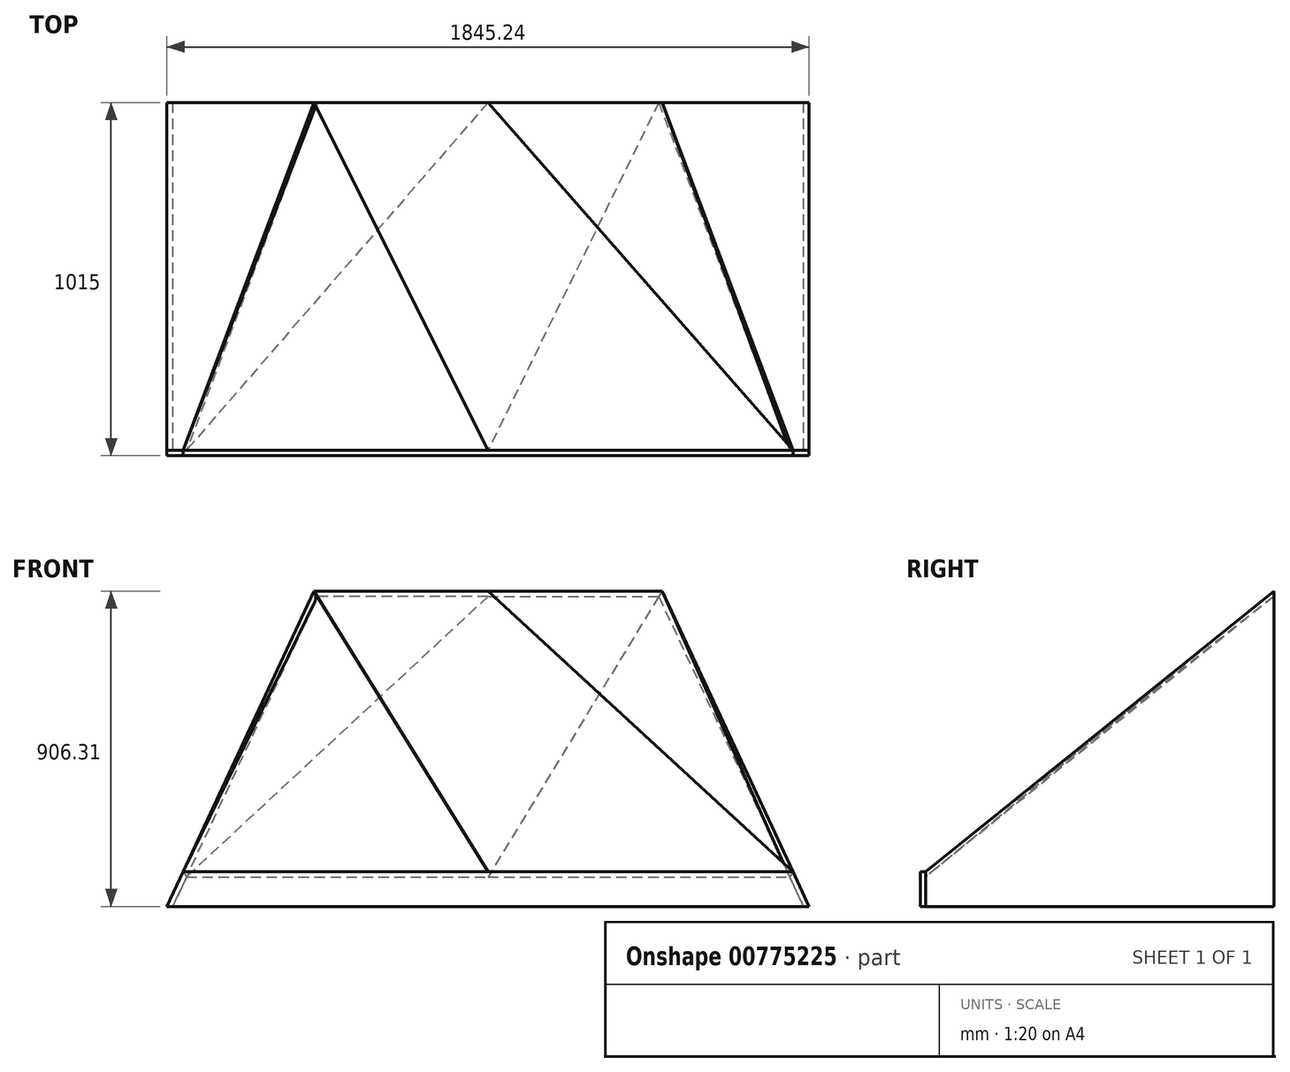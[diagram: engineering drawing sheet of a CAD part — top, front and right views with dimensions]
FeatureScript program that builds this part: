
annotation { "Feature Type Name" : "Feature", "Feature Type Description" : "" }
export const myFeature = defineFeature(function(context is Context, id is Id, definition is map)
    precondition{}
    {
        {
            var Q0;
            Q0=qCreatedBy(makeId("Front.planeOp"),FACE);
            cPlane(context, id + "F0", {"entities" : qUnion([Q0]), "cplaneType" : CPlaneType.OFFSET, "offset" : 1000 * mm, "width" : 150 * mm, "height" : 150 * mm});
        }
        {
            var Q0;
            Q0=qCreatedBy(makeId("Front.planeOp"),FACE);
            var sketch = newSketch(context, id + "F1", { "sketchPlane" : qUnion([Q0])});
            skLineSegment(sketch, "E0", {"start": v(0, 0) * mm, "end": v(-500, 0) * mm});
            skLineSegment(sketch, "E1", {"start": v(-500, 0) * mm, "end": v(-922.62, -906.3) * mm});
            skLineSegment(sketch, "E2", {"start": v(-922.62, -906.3) * mm, "end": v(0, -906.3) * mm});
            skLineSegment(sketch, "E3.MirrorCS", {"start": v(0, 0) * mm, "end": v(500, 0) * mm});
            skLineSegment(sketch, "E4.MirrorCS", {"start": v(500, 0) * mm, "end": v(922.62, -906.3) * mm});
            skLineSegment(sketch, "E5.MirrorCS", {"start": v(922.62, -906.3) * mm, "end": v(0, -906.3) * mm});
            skLineSegment(sketch, "E6.0", {"start": v(-490.44, -15) * mm, "end": v(-906.07, -906.3) * mm});
            skLineSegment(sketch, "E6.1", {"start": v(0, -15) * mm, "end": v(-490.44, -15) * mm});
            skLineSegment(sketch, "E6.2", {"start": v(0, -15) * mm, "end": v(490.44, -15) * mm});
            skLineSegment(sketch, "E6.3", {"start": v(490.44, -15) * mm, "end": v(906.07, -906.3) * mm});
            skLineSegment(sketch, "E7", {"start": v(-500, 0) * mm, "end": v(-490.44, -15) * mm});
            skLineSegment(sketch, "E8", {"start": v(500, 0) * mm, "end": v(490.44, -15) * mm});
            skSolve(sketch);
        }
        {
            var Q0;
            Q0=qCreatedBy(id+"F0.planeOp",FACE);
            var sketch = newSketch(context, id + "F2", { "sketchPlane" : qUnion([Q0])});
            skLineSegment(sketch, "E9.0", {"start": v(-875.99, -806.3) * mm, "end": v(-922.62, -906.3) * mm});
            skLineSegment(sketch, "E10.0", {"start": v(875.99, -806.3) * mm, "end": v(922.62, -906.3) * mm});
            skPoint(sketch, "E11.end.orphan", {"position": v(-720.34, -806.3) * mm});
            skPoint(sketch, "E12.orphan", {"position": v(-500, 0) * mm});
            skPoint(sketch, "E13.orphan", {"position": v(500, 0) * mm});
            skLineSegment(sketch, "E14", {"start": v(-875.99, -806.3) * mm, "end": v(875.99, -806.3) * mm});
            skLineSegment(sketch, "E15.0", {"start": v(866.43, -821.3) * mm, "end": v(906.07, -906.3) * mm});
            skLineSegment(sketch, "E15.1", {"start": v(-866.43, -821.3) * mm, "end": v(866.43, -821.3) * mm});
            skLineSegment(sketch, "E15.2", {"start": v(-866.43, -821.3) * mm, "end": v(-906.07, -906.3) * mm});
            skLineSegment(sketch, "E16", {"start": v(-875.99, -806.3) * mm, "end": v(-866.43, -821.3) * mm});
            skLineSegment(sketch, "E17", {"start": v(875.99, -806.3) * mm, "end": v(866.43, -821.3) * mm});
            skLineSegment(sketch, "E18", {"start": v(-922.62, -906.3) * mm, "end": v(-906.07, -906.3) * mm});
            skLineSegment(sketch, "E19", {"start": v(922.62, -906.3) * mm, "end": v(906.07, -906.3) * mm});
            skSolve(sketch);
        }
        {
            var Q0;
            {var subQ0=sQuery(id+"F1.wireOp",EDGE,"E4.MirrorCS");Q0=makeQuery(id+"F1.imprint","IMPRINT",FACE,{"disambiguationData":[TD([[makeQuery(id+"F1.imprint","IMPRINT",EDGE,{"derivedFrom":subQ0}),-1.0]])]});}
            var Q1;
            Q1=makeQuery(id+"F2.imprint","IMPRINT",FACE,{"disambiguationData":[TD([[makeQuery(id+"F2.imprint","IMPRINT",EDGE,{"derivedFrom":sQuery(id+"F2.wireOp",EDGE,"E10.0")}),-1.0]])]});
            loft(context, id + "F3", {"sheetProfilesArray" : [{ "sheetProfileEntities" : qUnion([Q0]) }, { "sheetProfileEntities" : qUnion([Q1]) }]});
        }
        {
            var Q0;
            {var subQ0=sQuery(id+"F1.wireOp",EDGE,"E1");Q0=makeQuery(id+"F1.imprint","IMPRINT",FACE,{"disambiguationData":[TD([[makeQuery(id+"F1.imprint","IMPRINT",EDGE,{"derivedFrom":subQ0}),1.0]])]});}
            var Q1;
            Q1=makeQuery(id+"F2.imprint","IMPRINT",FACE,{"disambiguationData":[TD([[makeQuery(id+"F2.imprint","IMPRINT",EDGE,{"derivedFrom":sQuery(id+"F2.wireOp",EDGE,"E9.0")}),1.0]])]});
            loft(context, id + "F4", {"sheetProfilesArray" : [{ "sheetProfileEntities" : qUnion([Q0]) }, { "sheetProfileEntities" : qUnion([Q1]) }]});
        }
        {
            var Q0;
            Q0=qCreatedBy(id+"F0.planeOp",FACE);
            var sketch = newSketch(context, id + "F5", { "sketchPlane" : qUnion([Q0])});
            skLineSegment(sketch, "E20.0", {"start": v(-875.99, -806.3) * mm, "end": v(-922.62, -906.3) * mm});
            skLineSegment(sketch, "E21.0", {"start": v(875.99, -806.3) * mm, "end": v(922.62, -906.3) * mm});
            skLineSegment(sketch, "E22", {"start": v(875.99, -806.3) * mm, "end": v(-875.99, -806.3) * mm});
            skLineSegment(sketch, "E23", {"start": v(-922.62, -906.3) * mm, "end": v(922.62, -906.3) * mm});
            skSolve(sketch);
        }
        {
            var Q0;
            Q0=makeQuery(id+"F5.imprint","IMPRINT",FACE,{"disambiguationData":[TD([[makeQuery(id+"F5.imprint","IMPRINT",EDGE,{"derivedFrom":sQuery(id+"F5.wireOp",EDGE,"E20.0")}),1.0]])]});
            extrude(context, id + "F6", {"entities" : qUnion([Q0]), "depth" : 15 * mm, "offsetDistance" : 25 * mm});
        }
        {
            var Q0;
            Q0=makeQuery(id+"F1.imprint","IMPRINT",FACE,{"disambiguationData":[TD([[makeQuery(id+"F1.imprint","IMPRINT",EDGE,{"derivedFrom":sQuery(id+"F1.wireOp",EDGE,"E0")}),1.0]])]});
            var Q1;
            Q1=makeQuery(id+"F2.imprint","IMPRINT",FACE,{"disambiguationData":[TD([[makeQuery(id+"F2.imprint","IMPRINT",EDGE,{"derivedFrom":sQuery(id+"F2.wireOp",EDGE,"E14")}),-1.0]])]});
            loft(context, id + "F7", {"sheetProfilesArray" : [{ "sheetProfileEntities" : qUnion([Q0]) }, { "sheetProfileEntities" : qUnion([Q1]) }]});
        }
    });
